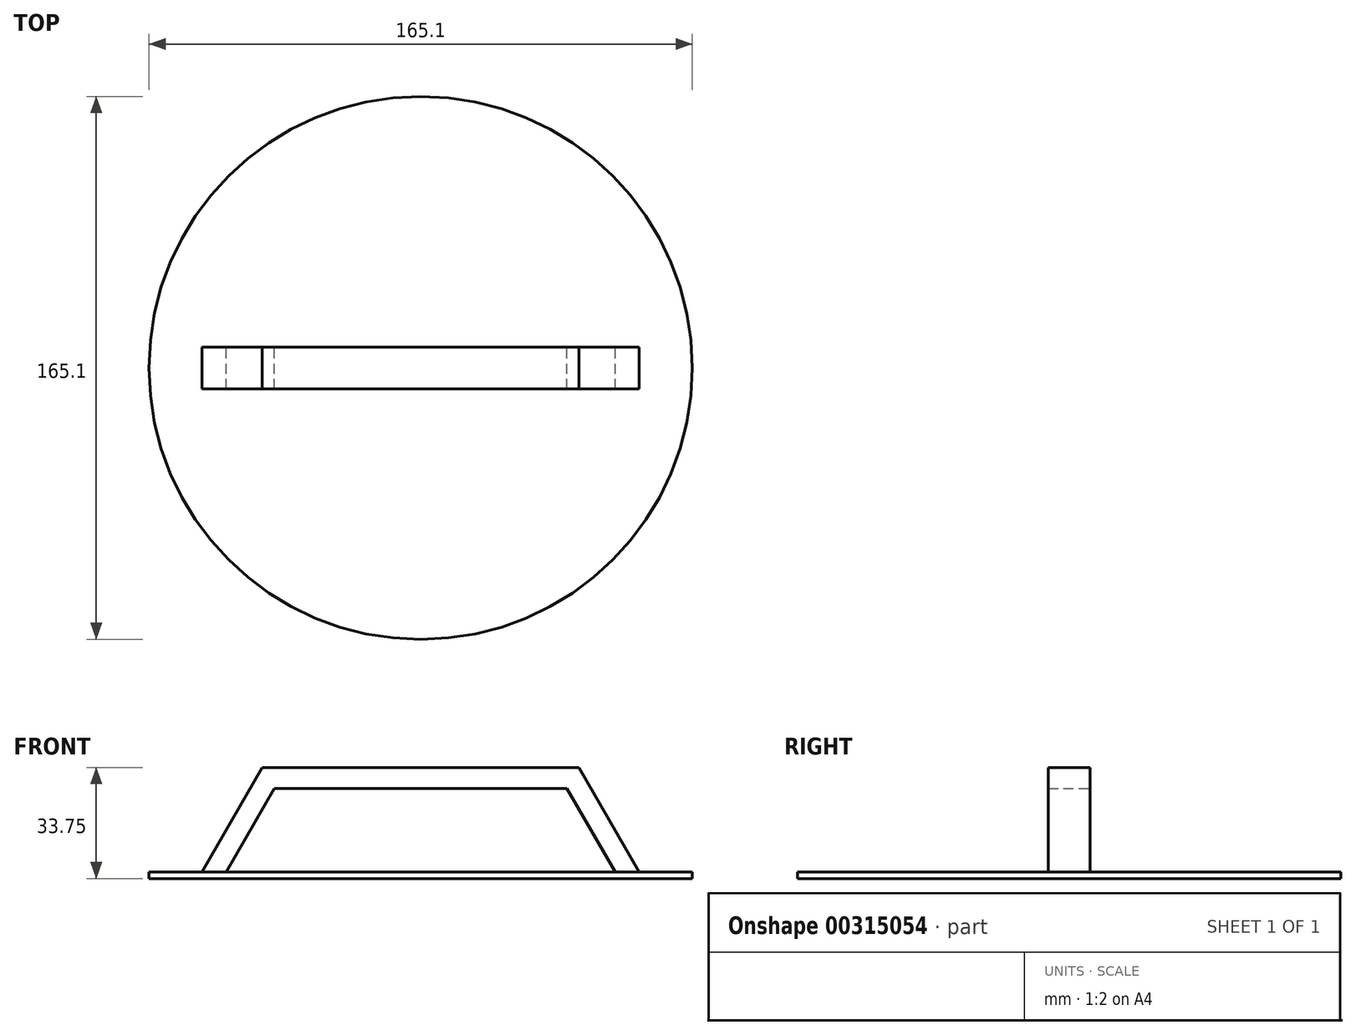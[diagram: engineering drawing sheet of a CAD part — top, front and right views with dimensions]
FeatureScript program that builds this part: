
annotation { "Feature Type Name" : "Feature", "Feature Type Description" : "" }
export const myFeature = defineFeature(function(context is Context, id is Id, definition is map)
    precondition{}
    {
        {
            var Q0;
            Q0=qCreatedBy(makeId("Top.planeOp"),FACE);
            var sketch = newSketch(context, id + "F0", { "sketchPlane" : qUnion([Q0])});
            skCircle(sketch, "E0", {"center": v(0, 0) * mm, "radius": 82.55 * mm});
            skSolve(sketch);
        }
        {
            var Q0;
            Q0 = qSketchRegion(id + "F0", true);
            extrude(context, id + "F1", {"entities" : qUnion([Q0]), "depth" : 2 * mm});
        }
        {
            var Q0;
            Q0=qCreatedBy(makeId("Front.planeOp"),FACE);
            var sketch = newSketch(context, id + "F2", { "sketchPlane" : qUnion([Q0])});
            skLineSegment(sketch, "E1.0.0", {"start": v(-82.55, 2) * mm, "end": v(82.55, 2) * mm, "construction": true});
            skLineSegment(sketch, "E2", {"start": v(82.55, 2) * mm, "end": v(82.55, 0) * mm, "construction": true});
            skLineSegment(sketch, "E3", {"start": v(-82.55, 0) * mm, "end": v(-82.55, 2) * mm, "construction": true});
            skLineSegment(sketch, "E4", {"start": v(-48.12, 33.75) * mm, "end": v(48.12, 33.75) * mm});
            skLineSegment(sketch, "E5", {"start": v(48.12, 33.75) * mm, "end": v(66.45, 2) * mm});
            skLineSegment(sketch, "E6", {"start": v(66.45, 2) * mm, "end": v(59.11, 2) * mm});
            skLineSegment(sketch, "E7", {"start": v(59.11, 2) * mm, "end": v(44.45, 27.4) * mm});
            skLineSegment(sketch, "E8", {"start": v(44.45, 27.4) * mm, "end": v(-44.45, 27.4) * mm});
            skLineSegment(sketch, "E9", {"start": v(-44.45, 27.4) * mm, "end": v(-59.11, 2) * mm});
            skLineSegment(sketch, "E10", {"start": v(-59.11, 2) * mm, "end": v(-66.45, 2) * mm});
            skLineSegment(sketch, "E11", {"start": v(-48.12, 33.75) * mm, "end": v(-66.45, 2) * mm});
            skSolve(sketch);
        }
        {
            var Q0;
            Q0 = qSketchRegion(id + "F2", true);
            extrude(context, id + "F3", {"entities" : qUnion([Q0]), "operationType" : NewBodyOperationType.ADD, "endBound" : BoundingType.SYMMETRIC, "depth" : 12.7 * mm});
        }
    });
